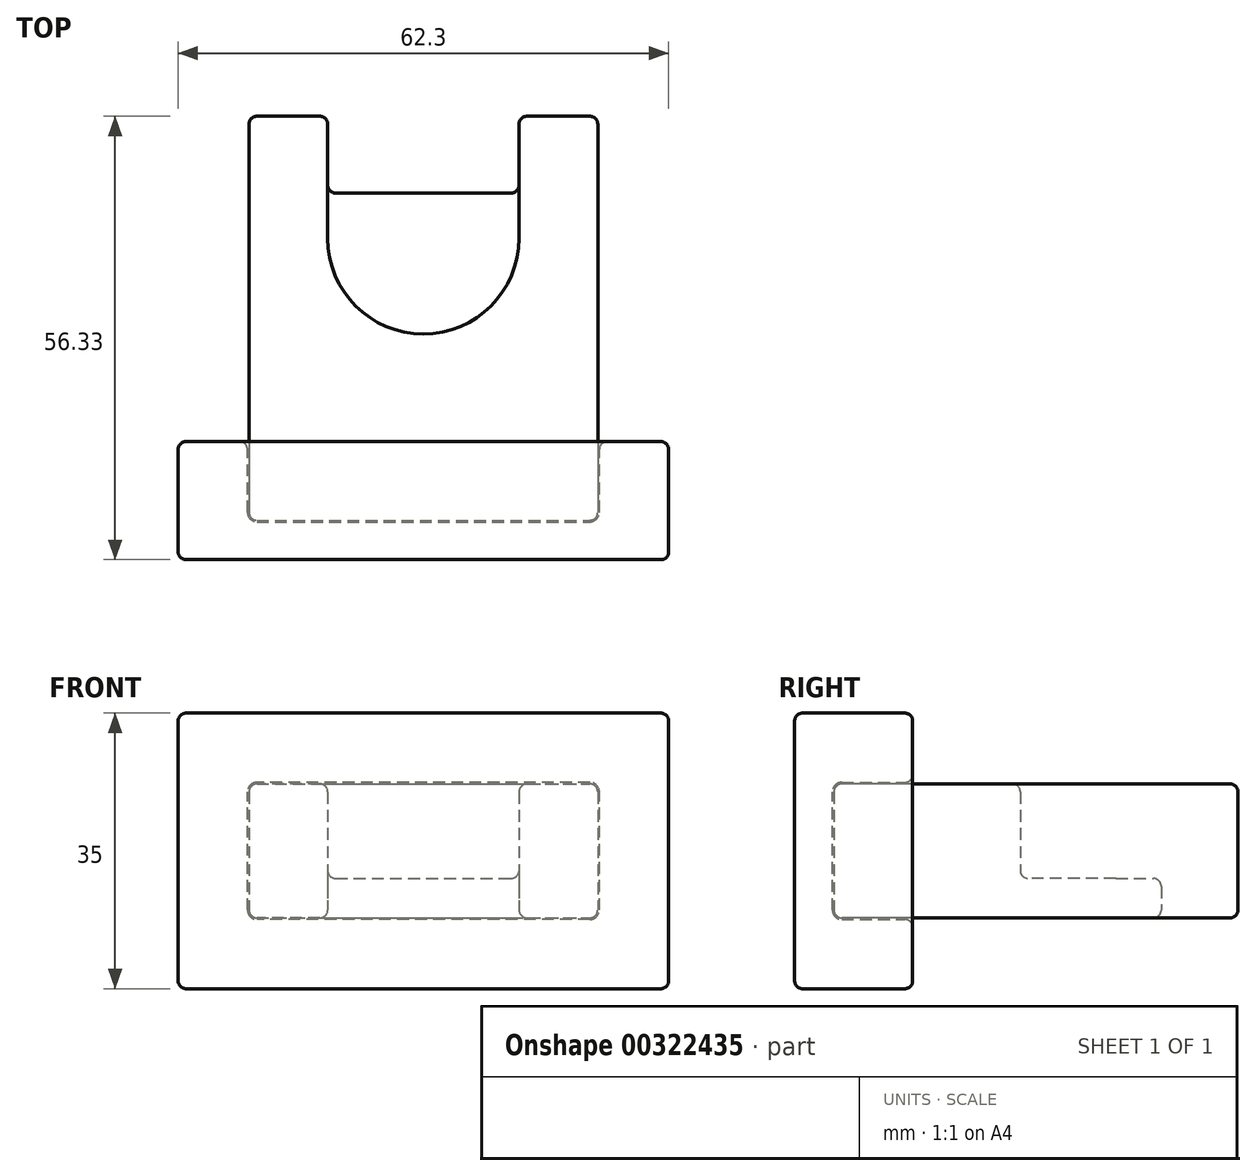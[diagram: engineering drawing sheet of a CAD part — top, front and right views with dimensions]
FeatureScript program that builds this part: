
annotation { "Feature Type Name" : "Feature", "Feature Type Description" : "" }
export const myFeature = defineFeature(function(context is Context, id is Id, definition is map)
    precondition{}
    {
        {
            var Q0;
            Q0=qCreatedBy(makeId("Top.planeOp"),FACE);
            var sketch = newSketch(context, id + "F0", { "sketchPlane" : qUnion([Q0])});
            skArc(sketch, "E0", {"start": v(-12.15, 0) * mm, "mid": v(0, -12.15) * mm, "end": v(12.15, 0) * mm});
            skLineSegment(sketch, "E1", {"start": v(-12.15, -25.82) * mm, "end": v(0, -25.82) * mm});
            skLineSegment(sketch, "E2", {"start": v(12.15, -25.82) * mm, "end": v(12.15, 0) * mm});
            skLineSegment(sketch, "E3", {"start": v(12.15, 0) * mm, "end": v(12.15, 15.51) * mm});
            skLineSegment(sketch, "E4", {"start": v(-12.15, 0) * mm, "end": v(-12.15, 15.51) * mm});
            skLineSegment(sketch, "E5", {"start": v(0, 0) * mm, "end": v(0, -38.3) * mm, "construction": true});
            skPoint(sketch, "E5.endSnap0", {"position": v(0, -25.82) * mm});
            skLineSegment(sketch, "E6", {"start": v(-12.15, 15.51) * mm, "end": v(-22.15, 15.51) * mm});
            skLineSegment(sketch, "E7", {"start": v(-22.15, 15.51) * mm, "end": v(-22.15, -35.82) * mm});
            skLineSegment(sketch, "E8", {"start": v(-22.15, -35.82) * mm, "end": v(0, -35.82) * mm});
            skLineSegment(sketch, "E9.MirrorCS", {"start": v(22.15, -35.82) * mm, "end": v(0, -35.82) * mm});
            skLineSegment(sketch, "E10.MirrorCS", {"start": v(22.15, 15.51) * mm, "end": v(22.15, -35.82) * mm});
            skLineSegment(sketch, "E11.MirrorCS", {"start": v(12.15, 15.51) * mm, "end": v(22.15, 15.51) * mm});
            skLineSegment(sketch, "E12", {"start": v(-12.15, 5.76) * mm, "end": v(12.15, 5.76) * mm});
            skSolve(sketch);
        }
        {
            var Q0;
            {var subQ0=sQuery(id+"F0.wireOp",EDGE,"E0");Q0=makeQuery(id+"F0.imprint","IMPRINT",FACE,{"disambiguationData":[TD([[makeQuery(id+"F0.imprint","IMPRINT",EDGE,{"derivedFrom":subQ0}),1.0]])]});}
            extrude(context, id + "F1", {"entities" : qUnion([Q0]), "depth" : 5 * mm});
        }
        {
            var Q0;
            {var subQ4=sQuery(id+"F0.wireOp",EDGE,"E0");Q0=makeQuery(id+"F0.imprint","IMPRINT",FACE,{"disambiguationData":[TD([[makeQuery(id+"F0.imprint","IMPRINT",EDGE,{"derivedFrom":subQ4}),-1.0]])]});}
            extrude(context, id + "F2", {"entities" : qUnion([Q0]), "operationType" : NewBodyOperationType.ADD, "depth" : 17 * mm});
        }
        {
            var Q0;
            Q0=makeQuery(id+"F2.opExtrude","CAP_FACE",FACE,{"disambiguationData":[OSD([sQuery(id+"F0.wireOp",EDGE,"E0"),sQuery(id+"F0.wireOp",EDGE,"E3"),sQuery(id+"F0.wireOp",EDGE,"E4"),sQuery(id+"F0.wireOp",EDGE,"E6"),sQuery(id+"F0.wireOp",EDGE,"E7"),sQuery(id+"F0.wireOp",EDGE,"E8"),sQuery(id+"F0.wireOp",EDGE,"E9.MirrorCS"),sQuery(id+"F0.wireOp",EDGE,"E10.MirrorCS"),sQuery(id+"F0.wireOp",EDGE,"E11.MirrorCS")])],"isStart":false});
            var Q1;
            Q1=makeQuery(id+"F2.opExtrude","SWEPT_FACE",FACE,{"disambiguationData":[OSD([sQuery(id+"F0.wireOp",EDGE,"E4")])]});
            var Q2;
            Q2=makeQuery(id+"F2.opExtrude","SWEPT_FACE",FACE,{"disambiguationData":[OSD([sQuery(id+"F0.wireOp",EDGE,"E3")])]});
            var Q3;
            Q3=makeQuery(id+"F1.opExtrude","SWEPT_FACE",FACE,{"disambiguationData":[OSD([sQuery(id+"F0.wireOp",EDGE,"E12")])]});
            var Q4;
            {var subQ0=sQuery(id+"F0.wireOp",EDGE,"E4");var subQ1=sQuery(id+"F0.wireOp",EDGE,"E3");var subQ2=sQuery(id+"F0.wireOp",EDGE,"E0");Q4=makeQuery(id+"F2.boolean.opBoolean","MERGE",FACE,{"derivedFrom":[makeQuery(id+"F1.opExtrude","CAP_FACE",FACE,{"disambiguationData":[OSD([subQ2,subQ1,subQ0,sQuery(id+"F0.wireOp",EDGE,"E12")])],"isStart":true}),makeQuery(id+"F2.opExtrude","CAP_FACE",FACE,{"disambiguationData":[OSD([subQ2,subQ1,subQ0,sQuery(id+"F0.wireOp",EDGE,"E6"),sQuery(id+"F0.wireOp",EDGE,"E7"),sQuery(id+"F0.wireOp",EDGE,"E8"),sQuery(id+"F0.wireOp",EDGE,"E9.MirrorCS"),sQuery(id+"F0.wireOp",EDGE,"E10.MirrorCS"),sQuery(id+"F0.wireOp",EDGE,"E11.MirrorCS")])],"isStart":true})]});}
            var Q5;
            Q5=makeQuery(id+"F2.opExtrude","SWEPT_FACE",FACE,{"disambiguationData":[OSD([sQuery(id+"F0.wireOp",EDGE,"E7")])]});
            var Q6;
            Q6=makeQuery(id+"F2.opExtrude","SWEPT_FACE",FACE,{"disambiguationData":[OSD([sQuery(id+"F0.wireOp",EDGE,"E8"),sQuery(id+"F0.wireOp",EDGE,"E9.MirrorCS")])]});
            var Q7;
            Q7=makeQuery(id+"F2.opExtrude","SWEPT_FACE",FACE,{"disambiguationData":[OSD([sQuery(id+"F0.wireOp",EDGE,"E10.MirrorCS")])]});
            fillet(context, id + "F3", {"entities" : qUnion([Q0, Q1, Q2, Q3, Q4, Q5, Q6, Q7]), "radius" : 1 * mm, "tangentPropagation" : true, "allowEdgeOverflow" : false});
        }
        {
            var Q0;
            Q0=makeQuery(id+"F2.opExtrude","SWEPT_FACE",FACE,{"disambiguationData":[OSD([sQuery(id+"F0.wireOp",EDGE,"E8"),sQuery(id+"F0.wireOp",EDGE,"E9.MirrorCS")])]});
            var sketch = newSketch(context, id + "F4", { "sketchPlane" : qUnion([Q0])});
            skLineSegment(sketch, "E13.0.0", {"start": v(-21.15, 16) * mm, "end": v(-21.15, 1) * mm});
            skLineSegment(sketch, "E13.0.1", {"start": v(-21.15, 1) * mm, "end": v(21.15, 1) * mm});
            skLineSegment(sketch, "E13.0.2", {"start": v(21.15, 1) * mm, "end": v(21.15, 16) * mm});
            skLineSegment(sketch, "E13.0.3", {"start": v(21.15, 16) * mm, "end": v(-21.15, 16) * mm});
            skLineSegment(sketch, "E14.0", {"start": v(-31.15, 26) * mm, "end": v(-31.15, -9) * mm});
            skLineSegment(sketch, "E14.1", {"start": v(31.15, 26) * mm, "end": v(-31.15, 26) * mm});
            skLineSegment(sketch, "E14.2", {"start": v(31.15, -9) * mm, "end": v(31.15, 26) * mm});
            skLineSegment(sketch, "E14.3", {"start": v(-31.15, -9) * mm, "end": v(31.15, -9) * mm});
            skSolve(sketch);
        }
        {
            var Q0;
            Q0=makeQuery(id+"F4.imprint","IMPRINT",FACE,{"disambiguationData":[TD([[makeQuery(id+"F4.imprint","IMPRINT",EDGE,{"derivedFrom":sQuery(id+"F4.wireOp",EDGE,"E13.0.0")}),-1.0]])]});
            var Q1;
            Q1=makeQuery(id+"F4.imprint","IMPRINT",FACE,{"disambiguationData":[TD([[makeQuery(id+"F4.imprint","IMPRINT",EDGE,{"derivedFrom":sQuery(id+"F4.wireOp",EDGE,"E13.0.0")}),1.0]])]});
            extrude(context, id + "F5", {"entities" : qUnion([Q0, Q1]), "depth" : 5 * mm, "hasSecondDirection" : true, "secondDirectionOppositeDirection" : true, "secondDirectionDepth" : 10 * mm});
        }
        {
            var Q0;
            Q0=makeQuery(id+"F1.opExtrude","SWEPT_BODY",BODY,{"disambiguationData":[OSD([sQuery(id+"F0.wireOp",EDGE,"E0"),sQuery(id+"F0.wireOp",EDGE,"E3"),sQuery(id+"F0.wireOp",EDGE,"E4"),sQuery(id+"F0.wireOp",EDGE,"E12")])]});
            var Q1;
            Q1=makeQuery(id+"F5.opExtrude","SWEPT_BODY",BODY,{"disambiguationData":[OSD([sQuery(id+"F4.wireOp",EDGE,"E14.0"),sQuery(id+"F4.wireOp",EDGE,"E14.1"),sQuery(id+"F4.wireOp",EDGE,"E14.2"),sQuery(id+"F4.wireOp",EDGE,"E14.3")])]});
            booleanBodies(context, id + "F6", {"operationType" : BooleanOperationType.SUBTRACTION, "tools" : qUnion([Q0]), "targets" : qUnion([Q1]), "offset" : true, "offsetAll" : true, "offsetDistance" : 0.2 * mm, "keepTools" : true});
        }
        {
            var Q0;
            Q0=makeQuery(id+"F5.opExtrude","CAP_FACE",FACE,{"disambiguationData":[OSD([sQuery(id+"F4.wireOp",EDGE,"E14.0"),sQuery(id+"F4.wireOp",EDGE,"E14.1"),sQuery(id+"F4.wireOp",EDGE,"E14.2"),sQuery(id+"F4.wireOp",EDGE,"E14.3")])],"isStart":true});
            var Q1;
            Q1=makeQuery(id+"F5.opExtrude","CAP_FACE",FACE,{"disambiguationData":[OSD([sQuery(id+"F4.wireOp",EDGE,"E14.0"),sQuery(id+"F4.wireOp",EDGE,"E14.1"),sQuery(id+"F4.wireOp",EDGE,"E14.2"),sQuery(id+"F4.wireOp",EDGE,"E14.3")])],"isStart":false});
            var Q2;
            Q2=makeQuery(id+"F5.opExtrude","SWEPT_FACE",FACE,{"disambiguationData":[OSD([sQuery(id+"F4.wireOp",EDGE,"E14.2")])]});
            var Q3;
            Q3=makeQuery(id+"F5.opExtrude","SWEPT_FACE",FACE,{"disambiguationData":[OSD([sQuery(id+"F4.wireOp",EDGE,"E14.1")])]});
            var Q4;
            Q4=makeQuery(id+"F5.opExtrude","SWEPT_FACE",FACE,{"disambiguationData":[OSD([sQuery(id+"F4.wireOp",EDGE,"E14.0")])]});
            var Q5;
            Q5=makeQuery(id+"F5.opExtrude","SWEPT_FACE",FACE,{"disambiguationData":[OSD([sQuery(id+"F4.wireOp",EDGE,"E14.3")])]});
            fillet(context, id + "F7", {"entities" : qUnion([Q0, Q1, Q2, Q3, Q4, Q5]), "radius" : 1 * mm, "tangentPropagation" : true, "allowEdgeOverflow" : false});
        }
    });
